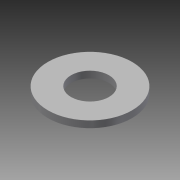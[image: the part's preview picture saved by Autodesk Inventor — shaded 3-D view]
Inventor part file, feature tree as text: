
AUTODESK INVENTOR PART (.ipt)
format: ipt  version: 2014 SP1 (Build 180222100, 222)  size: 75,776 bytes
history: native  units: in
note: dims shown in document units (in); Inventor stores cm internally (conversion verified against a paired STEP export)
features: extrude x1, sketch x1
ambient origin geometry x8: Origin, YZ Plane, XZ Plane, XY Plane, X Axis, Y Axis, Z Axis, Center Point
bodies: Solid1 (feature_tree)
feature tree (2):
  extrude  "Extrusion1"  Depth=0.05in
  sketch  "Sketch1"  dims[d0=0.2812in d1=0.625in d2=0.05in d3=0.0in]
